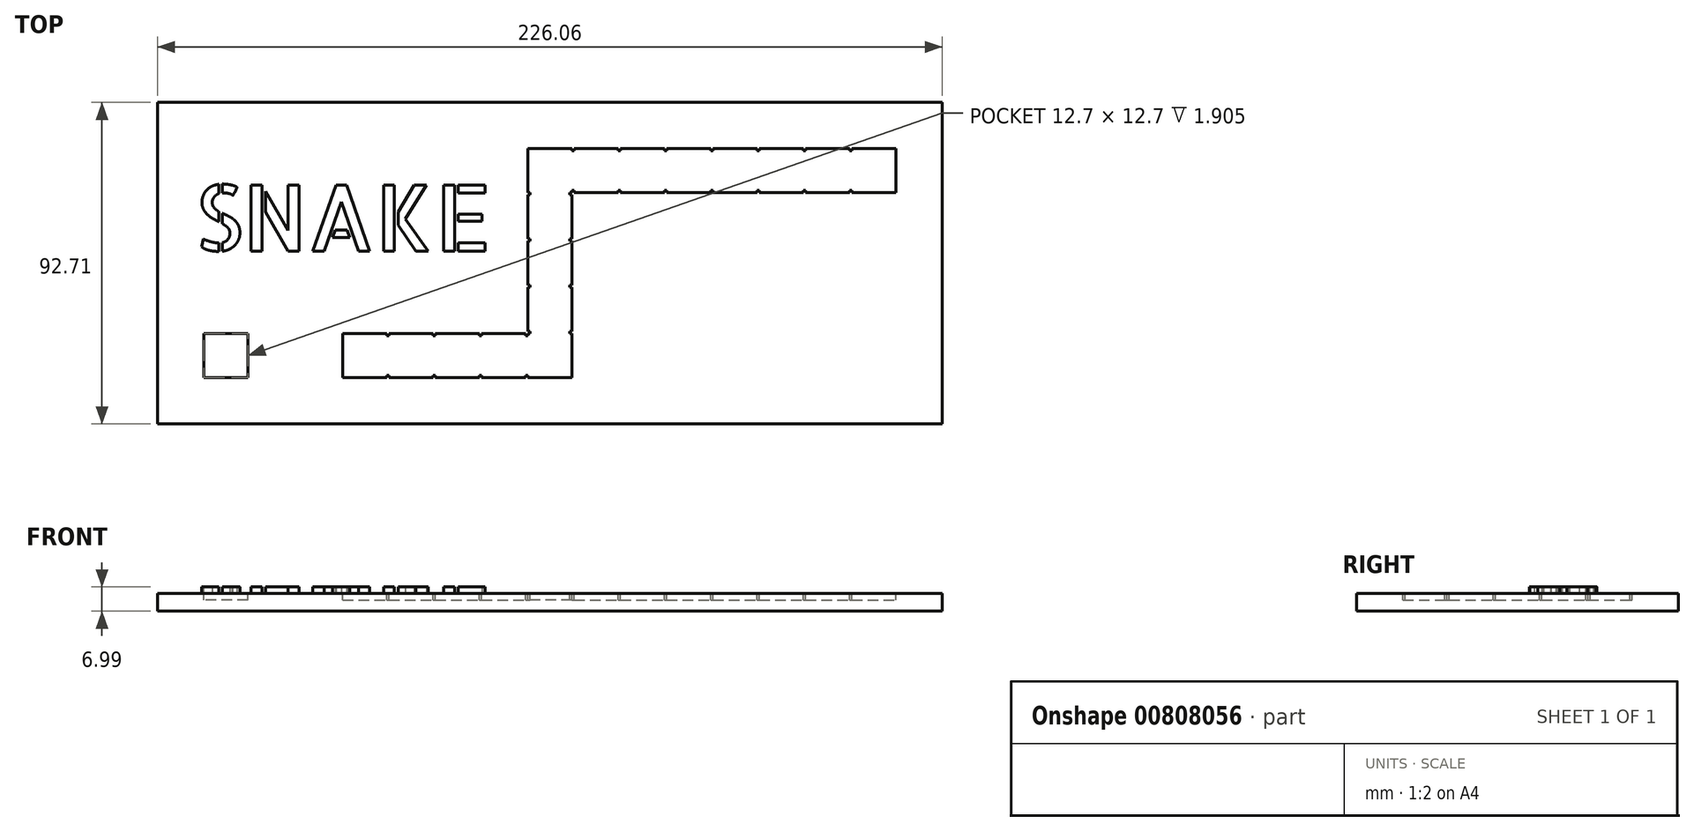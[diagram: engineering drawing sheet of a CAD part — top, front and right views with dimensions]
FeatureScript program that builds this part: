
annotation { "Feature Type Name" : "Feature", "Feature Type Description" : "" }
export const myFeature = defineFeature(function(context is Context, id is Id, definition is map)
    precondition{}
    {
        {
            var Q0;
            Q0=qCreatedBy(makeId("Top.planeOp"),FACE);
            var sketch = newSketch(context, id + "F0", { "sketchPlane" : qUnion([Q0])});
            skLineSegment(sketch, "E0.bottom", {"start": v(-132.08, 0) * mm, "end": v(-106.68, 0) * mm});
            skLineSegment(sketch, "E0.top", {"start": v(-132.08, 25.4) * mm, "end": v(-106.68, 25.4) * mm});
            skLineSegment(sketch, "E0.left", {"start": v(-132.08, 0) * mm, "end": v(-132.08, 25.4) * mm});
            skLineSegment(sketch, "E0.right", {"start": v(-106.68, 0) * mm, "end": v(-106.68, 25.4) * mm});
            skLineSegment(sketch, "E1.bottom", {"start": v(-106.68, 24.13) * mm, "end": v(-105.41, 24.13) * mm});
            skLineSegment(sketch, "E1.top", {"start": v(-106.68, 1.27) * mm, "end": v(-105.41, 1.27) * mm});
            skLineSegment(sketch, "E1.left", {"start": v(-106.68, 24.13) * mm, "end": v(-106.68, 1.27) * mm});
            skLineSegment(sketch, "E1.right", {"start": v(-105.41, 24.13) * mm, "end": v(-105.41, 1.27) * mm});
            skLineSegment(sketch, "E2", {"start": v(-106.68, 25.4) * mm, "end": v(-106.68, 24.13) * mm});
            skLineSegment(sketch, "E3", {"start": v(-106.68, 0) * mm, "end": v(-106.68, 1.27) * mm});
            skLineSegment(sketch, "E4.bottom", {"start": v(-105.41, 0) * mm, "end": v(-80.01, 0) * mm});
            skLineSegment(sketch, "E4.top", {"start": v(-105.41, 25.4) * mm, "end": v(-80.01, 25.4) * mm});
            skLineSegment(sketch, "E4.left", {"start": v(-105.41, 0) * mm, "end": v(-105.41, 25.4) * mm});
            skLineSegment(sketch, "E4.right", {"start": v(-80.01, 0) * mm, "end": v(-80.01, 25.4) * mm});
            skLineSegment(sketch, "E5.bottom", {"start": v(-80.01, 24.13) * mm, "end": v(-78.74, 24.13) * mm});
            skLineSegment(sketch, "E5.top", {"start": v(-80.01, 1.27) * mm, "end": v(-78.74, 1.27) * mm});
            skLineSegment(sketch, "E5.left", {"start": v(-80.01, 24.13) * mm, "end": v(-80.01, 1.27) * mm});
            skLineSegment(sketch, "E5.right", {"start": v(-78.74, 24.13) * mm, "end": v(-78.74, 1.27) * mm});
            skLineSegment(sketch, "E6", {"start": v(-80.01, 25.4) * mm, "end": v(-80.01, 24.13) * mm});
            skLineSegment(sketch, "E7", {"start": v(-80.01, 0) * mm, "end": v(-80.01, 1.27) * mm});
            skLineSegment(sketch, "E8.bottom", {"start": v(-78.74, 0) * mm, "end": v(-53.34, 0) * mm});
            skLineSegment(sketch, "E8.top", {"start": v(-78.74, 25.4) * mm, "end": v(-53.34, 25.4) * mm});
            skLineSegment(sketch, "E8.left", {"start": v(-78.74, 0) * mm, "end": v(-78.74, 25.4) * mm});
            skLineSegment(sketch, "E8.right", {"start": v(-53.34, 0) * mm, "end": v(-53.34, 25.4) * mm});
            skLineSegment(sketch, "E9.bottom", {"start": v(-53.34, 24.13) * mm, "end": v(-52.07, 24.13) * mm});
            skLineSegment(sketch, "E9.top", {"start": v(-53.34, 1.27) * mm, "end": v(-52.07, 1.27) * mm});
            skLineSegment(sketch, "E9.left", {"start": v(-53.34, 24.13) * mm, "end": v(-53.34, 1.27) * mm});
            skLineSegment(sketch, "E9.right", {"start": v(-52.07, 24.13) * mm, "end": v(-52.07, 1.27) * mm});
            skLineSegment(sketch, "E10", {"start": v(-53.34, 25.4) * mm, "end": v(-53.34, 24.13) * mm});
            skLineSegment(sketch, "E11", {"start": v(-53.34, 0) * mm, "end": v(-53.34, 1.27) * mm});
            skLineSegment(sketch, "E12.bottom", {"start": v(-52.07, 0) * mm, "end": v(-26.67, 0) * mm});
            skLineSegment(sketch, "E12.top", {"start": v(-52.07, 25.4) * mm, "end": v(-26.67, 25.4) * mm});
            skLineSegment(sketch, "E12.left", {"start": v(-52.07, 0) * mm, "end": v(-52.07, 25.4) * mm});
            skLineSegment(sketch, "E12.right", {"start": v(-26.67, 0) * mm, "end": v(-26.67, 25.4) * mm});
            skLineSegment(sketch, "E13.bottom", {"start": v(-26.67, 24.13) * mm, "end": v(-25.4, 24.13) * mm});
            skLineSegment(sketch, "E13.top", {"start": v(-26.67, 1.27) * mm, "end": v(-25.4, 1.27) * mm});
            skLineSegment(sketch, "E13.left", {"start": v(-26.67, 24.13) * mm, "end": v(-26.67, 1.27) * mm});
            skLineSegment(sketch, "E13.right", {"start": v(-25.4, 24.13) * mm, "end": v(-25.4, 1.27) * mm});
            skLineSegment(sketch, "E14", {"start": v(-26.67, 25.4) * mm, "end": v(-26.67, 24.13) * mm});
            skLineSegment(sketch, "E15", {"start": v(-26.67, 0) * mm, "end": v(-26.67, 1.27) * mm});
            skLineSegment(sketch, "E16.bottom", {"start": v(0, 0) * mm, "end": v(0, 25.4) * mm});
            skLineSegment(sketch, "E16.top", {"start": v(-25.4, 0) * mm, "end": v(-25.4, 25.4) * mm});
            skLineSegment(sketch, "E16.left", {"start": v(0, 0) * mm, "end": v(-25.4, 0) * mm});
            skLineSegment(sketch, "E16.right", {"start": v(0, 25.4) * mm, "end": v(-25.4, 25.4) * mm});
            skLineSegment(sketch, "E17.bottom", {"start": v(-24.13, 25.4) * mm, "end": v(-24.13, 26.67) * mm});
            skLineSegment(sketch, "E17.top", {"start": v(-1.27, 25.4) * mm, "end": v(-1.27, 26.67) * mm});
            skLineSegment(sketch, "E17.left", {"start": v(-24.13, 25.4) * mm, "end": v(-1.27, 25.4) * mm});
            skLineSegment(sketch, "E17.right", {"start": v(-24.13, 26.67) * mm, "end": v(-1.27, 26.67) * mm});
            skLineSegment(sketch, "E18", {"start": v(-25.4, 25.4) * mm, "end": v(-24.13, 25.4) * mm});
            skLineSegment(sketch, "E19", {"start": v(0, 25.4) * mm, "end": v(-1.27, 25.4) * mm});
            skLineSegment(sketch, "E20.bottom", {"start": v(0, 26.67) * mm, "end": v(0, 52.07) * mm});
            skLineSegment(sketch, "E20.top", {"start": v(-25.4, 26.67) * mm, "end": v(-25.4, 52.07) * mm});
            skLineSegment(sketch, "E20.left", {"start": v(0, 26.67) * mm, "end": v(-25.4, 26.67) * mm});
            skLineSegment(sketch, "E20.right", {"start": v(0, 52.07) * mm, "end": v(-25.4, 52.07) * mm});
            skLineSegment(sketch, "E21.bottom", {"start": v(-24.13, 52.07) * mm, "end": v(-24.13, 53.34) * mm});
            skLineSegment(sketch, "E21.top", {"start": v(-1.27, 52.07) * mm, "end": v(-1.27, 53.34) * mm});
            skLineSegment(sketch, "E21.left", {"start": v(-24.13, 52.07) * mm, "end": v(-1.27, 52.07) * mm});
            skLineSegment(sketch, "E21.right", {"start": v(-24.13, 53.34) * mm, "end": v(-1.27, 53.34) * mm});
            skLineSegment(sketch, "E22", {"start": v(-25.4, 52.07) * mm, "end": v(-24.13, 52.07) * mm});
            skLineSegment(sketch, "E23", {"start": v(0, 52.07) * mm, "end": v(-1.27, 52.07) * mm});
            skLineSegment(sketch, "E24.bottom", {"start": v(0, 53.34) * mm, "end": v(0, 78.74) * mm});
            skLineSegment(sketch, "E24.top", {"start": v(-25.4, 53.34) * mm, "end": v(-25.4, 78.74) * mm});
            skLineSegment(sketch, "E24.left", {"start": v(0, 53.34) * mm, "end": v(-25.4, 53.34) * mm});
            skLineSegment(sketch, "E24.right", {"start": v(0, 78.74) * mm, "end": v(-25.4, 78.74) * mm});
            skLineSegment(sketch, "E25.bottom", {"start": v(-24.13, 78.74) * mm, "end": v(-24.13, 80) * mm});
            skLineSegment(sketch, "E25.top", {"start": v(-1.27, 78.74) * mm, "end": v(-1.27, 80) * mm});
            skLineSegment(sketch, "E25.left", {"start": v(-24.13, 78.74) * mm, "end": v(-1.27, 78.74) * mm});
            skLineSegment(sketch, "E25.right", {"start": v(-24.13, 80) * mm, "end": v(-1.27, 80) * mm});
            skLineSegment(sketch, "E26", {"start": v(-25.4, 78.74) * mm, "end": v(-24.13, 78.74) * mm});
            skLineSegment(sketch, "E27", {"start": v(0, 78.74) * mm, "end": v(-1.27, 78.74) * mm});
            skLineSegment(sketch, "E28.bottom", {"start": v(0, 80) * mm, "end": v(0, 105.4) * mm});
            skLineSegment(sketch, "E28.top", {"start": v(-25.4, 80) * mm, "end": v(-25.4, 105.4) * mm});
            skLineSegment(sketch, "E28.left", {"start": v(0, 80) * mm, "end": v(-25.4, 80) * mm});
            skLineSegment(sketch, "E28.right", {"start": v(0, 105.4) * mm, "end": v(-25.4, 105.4) * mm});
            skLineSegment(sketch, "E29.bottom", {"start": v(-24.13, 105.4) * mm, "end": v(-24.13, 106.68) * mm});
            skLineSegment(sketch, "E29.top", {"start": v(-1.27, 105.4) * mm, "end": v(-1.27, 106.68) * mm});
            skLineSegment(sketch, "E29.left", {"start": v(-24.13, 105.4) * mm, "end": v(-1.27, 105.4) * mm});
            skLineSegment(sketch, "E29.right", {"start": v(-24.13, 106.68) * mm, "end": v(-1.27, 106.68) * mm});
            skLineSegment(sketch, "E30", {"start": v(-25.4, 105.4) * mm, "end": v(-24.13, 105.4) * mm});
            skLineSegment(sketch, "E31", {"start": v(0, 105.4) * mm, "end": v(-1.27, 105.4) * mm});
            skLineSegment(sketch, "E32", {"start": v(-25.4, 1.27) * mm, "end": v(-25.4, 12.7) * mm});
            skLineSegment(sketch, "E33", {"start": v(-25.4, 12.7) * mm, "end": v(-26.67, 12.7) * mm});
            skLineSegment(sketch, "E34.bottom", {"start": v(-25.4, 106.68) * mm, "end": v(0, 106.68) * mm});
            skLineSegment(sketch, "E34.top", {"start": v(-25.4, 132.08) * mm, "end": v(0, 132.08) * mm});
            skLineSegment(sketch, "E34.left", {"start": v(-25.4, 106.68) * mm, "end": v(-25.4, 132.08) * mm});
            skLineSegment(sketch, "E34.right", {"start": v(0, 106.68) * mm, "end": v(0, 132.08) * mm});
            skLineSegment(sketch, "E35.bottom", {"start": v(0, 130.8) * mm, "end": v(1.27, 130.8) * mm});
            skLineSegment(sketch, "E35.top", {"start": v(0, 107.95) * mm, "end": v(1.27, 107.95) * mm});
            skLineSegment(sketch, "E35.left", {"start": v(0, 130.8) * mm, "end": v(0, 107.95) * mm});
            skLineSegment(sketch, "E35.right", {"start": v(1.27, 130.8) * mm, "end": v(1.27, 107.95) * mm});
            skLineSegment(sketch, "E36", {"start": v(0, 132.08) * mm, "end": v(0, 130.8) * mm});
            skLineSegment(sketch, "E37", {"start": v(0, 106.68) * mm, "end": v(0, 107.95) * mm});
            skLineSegment(sketch, "E38.bottom", {"start": v(1.27, 106.68) * mm, "end": v(26.67, 106.68) * mm});
            skLineSegment(sketch, "E38.top", {"start": v(1.27, 132.08) * mm, "end": v(26.67, 132.08) * mm});
            skLineSegment(sketch, "E38.left", {"start": v(1.27, 106.68) * mm, "end": v(1.27, 132.08) * mm});
            skLineSegment(sketch, "E38.right", {"start": v(26.67, 106.68) * mm, "end": v(26.67, 132.08) * mm});
            skLineSegment(sketch, "E39.bottom", {"start": v(26.67, 130.8) * mm, "end": v(27.94, 130.8) * mm});
            skLineSegment(sketch, "E39.top", {"start": v(26.67, 107.95) * mm, "end": v(27.94, 107.95) * mm});
            skLineSegment(sketch, "E39.left", {"start": v(26.67, 130.8) * mm, "end": v(26.67, 107.95) * mm});
            skLineSegment(sketch, "E39.right", {"start": v(27.94, 130.8) * mm, "end": v(27.94, 107.95) * mm});
            skLineSegment(sketch, "E40", {"start": v(26.67, 132.08) * mm, "end": v(26.67, 130.8) * mm});
            skLineSegment(sketch, "E41", {"start": v(26.67, 106.68) * mm, "end": v(26.67, 107.95) * mm});
            skLineSegment(sketch, "E42.bottom", {"start": v(27.94, 106.68) * mm, "end": v(53.34, 106.68) * mm});
            skLineSegment(sketch, "E42.top", {"start": v(27.94, 132.08) * mm, "end": v(53.34, 132.08) * mm});
            skLineSegment(sketch, "E42.left", {"start": v(27.94, 106.68) * mm, "end": v(27.94, 132.08) * mm});
            skLineSegment(sketch, "E42.right", {"start": v(53.34, 106.68) * mm, "end": v(53.34, 132.08) * mm});
            skLineSegment(sketch, "E43.bottom", {"start": v(53.34, 130.8) * mm, "end": v(54.6, 130.8) * mm});
            skLineSegment(sketch, "E43.top", {"start": v(53.34, 107.95) * mm, "end": v(54.6, 107.95) * mm});
            skLineSegment(sketch, "E43.left", {"start": v(53.34, 130.8) * mm, "end": v(53.34, 107.95) * mm});
            skLineSegment(sketch, "E43.right", {"start": v(54.6, 130.8) * mm, "end": v(54.6, 107.95) * mm});
            skLineSegment(sketch, "E44", {"start": v(53.34, 132.08) * mm, "end": v(53.34, 130.8) * mm});
            skLineSegment(sketch, "E45", {"start": v(53.34, 106.68) * mm, "end": v(53.34, 107.95) * mm});
            skLineSegment(sketch, "E46.bottom", {"start": v(54.6, 106.68) * mm, "end": v(80, 106.68) * mm});
            skLineSegment(sketch, "E46.top", {"start": v(54.6, 132.08) * mm, "end": v(80, 132.08) * mm});
            skLineSegment(sketch, "E46.left", {"start": v(54.6, 106.68) * mm, "end": v(54.6, 132.08) * mm});
            skLineSegment(sketch, "E46.right", {"start": v(80, 106.68) * mm, "end": v(80, 132.08) * mm});
            skLineSegment(sketch, "E47.bottom", {"start": v(80, 130.8) * mm, "end": v(81.28, 130.8) * mm});
            skLineSegment(sketch, "E47.top", {"start": v(80, 107.95) * mm, "end": v(81.28, 107.95) * mm});
            skLineSegment(sketch, "E47.left", {"start": v(80, 130.8) * mm, "end": v(80, 107.95) * mm});
            skLineSegment(sketch, "E47.right", {"start": v(81.28, 130.8) * mm, "end": v(81.28, 107.95) * mm});
            skLineSegment(sketch, "E48", {"start": v(80, 132.08) * mm, "end": v(80, 130.8) * mm});
            skLineSegment(sketch, "E49", {"start": v(80, 106.68) * mm, "end": v(80, 107.95) * mm});
            skLineSegment(sketch, "E50.bottom", {"start": v(81.28, 106.68) * mm, "end": v(106.68, 106.68) * mm});
            skLineSegment(sketch, "E50.top", {"start": v(81.28, 132.08) * mm, "end": v(106.68, 132.08) * mm});
            skLineSegment(sketch, "E50.left", {"start": v(81.28, 106.68) * mm, "end": v(81.28, 132.08) * mm});
            skLineSegment(sketch, "E50.right", {"start": v(106.68, 106.68) * mm, "end": v(106.68, 132.08) * mm});
            skLineSegment(sketch, "E51.bottom", {"start": v(106.68, 130.8) * mm, "end": v(107.95, 130.8) * mm});
            skLineSegment(sketch, "E51.top", {"start": v(106.68, 107.95) * mm, "end": v(107.95, 107.95) * mm});
            skLineSegment(sketch, "E51.left", {"start": v(106.68, 130.8) * mm, "end": v(106.68, 107.95) * mm});
            skLineSegment(sketch, "E51.right", {"start": v(107.95, 130.8) * mm, "end": v(107.95, 107.95) * mm});
            skLineSegment(sketch, "E52", {"start": v(106.68, 132.08) * mm, "end": v(106.68, 130.8) * mm});
            skLineSegment(sketch, "E53", {"start": v(106.68, 106.68) * mm, "end": v(106.68, 107.95) * mm});
            skLineSegment(sketch, "E54.bottom", {"start": v(107.95, 106.68) * mm, "end": v(133.35, 106.68) * mm});
            skLineSegment(sketch, "E54.top", {"start": v(107.95, 132.08) * mm, "end": v(133.35, 132.08) * mm});
            skLineSegment(sketch, "E54.left", {"start": v(107.95, 106.68) * mm, "end": v(107.95, 132.08) * mm});
            skLineSegment(sketch, "E54.right", {"start": v(133.35, 106.68) * mm, "end": v(133.35, 132.08) * mm});
            skLineSegment(sketch, "E55.bottom", {"start": v(133.35, 130.8) * mm, "end": v(134.62, 130.8) * mm});
            skLineSegment(sketch, "E55.top", {"start": v(133.35, 107.95) * mm, "end": v(134.62, 107.95) * mm});
            skLineSegment(sketch, "E55.left", {"start": v(133.35, 130.8) * mm, "end": v(133.35, 107.95) * mm});
            skLineSegment(sketch, "E55.right", {"start": v(134.62, 130.8) * mm, "end": v(134.62, 107.95) * mm});
            skLineSegment(sketch, "E56", {"start": v(133.35, 132.08) * mm, "end": v(133.35, 130.8) * mm});
            skLineSegment(sketch, "E57", {"start": v(133.35, 106.68) * mm, "end": v(133.35, 107.95) * mm});
            skLineSegment(sketch, "E58.bottom", {"start": v(134.62, 106.68) * mm, "end": v(160.02, 106.68) * mm});
            skLineSegment(sketch, "E58.top", {"start": v(134.62, 132.08) * mm, "end": v(160.02, 132.08) * mm});
            skLineSegment(sketch, "E58.left", {"start": v(134.62, 106.68) * mm, "end": v(134.62, 132.08) * mm});
            skLineSegment(sketch, "E58.right", {"start": v(160.02, 106.68) * mm, "end": v(160.02, 132.08) * mm});
            skLineSegment(sketch, "E59.bottom", {"start": v(160.02, 130.8) * mm, "end": v(161.29, 130.8) * mm});
            skLineSegment(sketch, "E59.top", {"start": v(160.02, 107.95) * mm, "end": v(161.29, 107.95) * mm});
            skLineSegment(sketch, "E59.left", {"start": v(160.02, 130.8) * mm, "end": v(160.02, 107.95) * mm});
            skLineSegment(sketch, "E59.right", {"start": v(161.29, 130.8) * mm, "end": v(161.29, 107.95) * mm});
            skLineSegment(sketch, "E60", {"start": v(160.02, 132.08) * mm, "end": v(160.02, 130.8) * mm});
            skLineSegment(sketch, "E61", {"start": v(160.02, 106.68) * mm, "end": v(160.02, 107.95) * mm});
            skLineSegment(sketch, "E62.bottom", {"start": v(161.29, 106.68) * mm, "end": v(186.69, 106.68) * mm});
            skLineSegment(sketch, "E62.top", {"start": v(161.29, 132.08) * mm, "end": v(186.7, 132.08) * mm});
            skLineSegment(sketch, "E62.left", {"start": v(161.29, 106.68) * mm, "end": v(161.29, 132.08) * mm});
            skLineSegment(sketch, "E62.right", {"start": v(186.7, 106.68) * mm, "end": v(186.7, 132.08) * mm});
            skLineSegment(sketch, "E63.left", {"start": v(186.7, 130.8) * mm, "end": v(186.7, 42.8) * mm});
            skLineSegment(sketch, "E64", {"start": v(186.7, 132.08) * mm, "end": v(186.7, 130.8) * mm});
            skLineSegment(sketch, "E65", {"start": v(186.7, 42.8) * mm, "end": v(186.7, 106.68) * mm});
            skLineSegment(sketch, "E66.bottom", {"start": v(213.36, -26.67) * mm, "end": v(-238.76, -26.67) * mm});
            skLineSegment(sketch, "E66.top", {"start": v(213.36, 158.75) * mm, "end": v(-238.76, 158.75) * mm});
            skLineSegment(sketch, "E66.left", {"start": v(213.36, -26.67) * mm, "end": v(213.36, 158.75) * mm});
            skLineSegment(sketch, "E66.right", {"start": v(-238.76, -26.67) * mm, "end": v(-238.76, 158.75) * mm});
            skLineSegment(sketch, "E67.bottom", {"start": v(-186.7, 25.4) * mm, "end": v(-212.1, 25.4) * mm});
            skLineSegment(sketch, "E67.top", {"start": v(-186.7, 0) * mm, "end": v(-212.1, 0) * mm});
            skLineSegment(sketch, "E67.left", {"start": v(-186.7, 25.4) * mm, "end": v(-186.7, 0) * mm});
            skLineSegment(sketch, "E67.right", {"start": v(-212.1, 25.4) * mm, "end": v(-212.1, 0) * mm});
            skText(sketch, "E68", { "text": "SNAKE", "fontName": "AllertaStencil-Regular.ttf"});
            skLineSegment(sketch, "E69", {"start": v(-217.6, 73.02) * mm, "end": v(-238.76, 73.02) * mm});
            skLineSegment(sketch, "E70", {"start": v(-46.57, 111.12) * mm, "end": v(-25.4, 111.12) * mm});
            skLineSegment(sketch, "E71", {"start": v(-132.08, 111.12) * mm, "end": v(-132.08, 158.75) * mm});
            skLineSegment(sketch, "E72", {"start": v(-132.08, 25.4) * mm, "end": v(-132.08, 73.02) * mm});
            const initialGuessF0  = {"E68": [-0.2176, 0.07302, 1, 0, 0.0381]};
            skSetInitialGuess(sketch, initialGuessF0);
            skSolve(sketch);
        }
        {
            var Q0;
            {var subQ3=sQuery(id+"F0.wireOp",EDGE,"E28.bottom");Q0=makeQuery(id+"F0.imprint","IMPRINT",FACE,{"disambiguationData":[TD([[makeQuery(id+"F0.imprint","IMPRINT",EDGE,{"derivedFrom":subQ3}),1.0]])]});}
            var Q1;
            Q1=makeQuery(id+"F0.imprint","IMPRINT",FACE,{"disambiguationData":[TD([[makeQuery(id+"F0.imprint","IMPRINT",EDGE,{"derivedFrom":sQuery(id+"F0.wireOp",EDGE,"E68.sketch_text.stroke-72")}),-1.0]])]});
            var Q2;
            Q2=makeQuery(id+"F0.imprint","IMPRINT",FACE,{"disambiguationData":[TD([[makeQuery(id+"F0.imprint","IMPRINT",EDGE,{"derivedFrom":sQuery(id+"F0.wireOp",EDGE,"E68.sketch_text.stroke-76")}),-1.0]])]});
            var Q3;
            {var subQ3=sQuery(id+"F0.wireOp",EDGE,"E24.bottom");Q3=makeQuery(id+"F0.imprint","IMPRINT",FACE,{"disambiguationData":[TD([[makeQuery(id+"F0.imprint","IMPRINT",EDGE,{"derivedFrom":subQ3}),1.0]])]});}
            var Q4;
            {var subQ3=sQuery(id+"F0.wireOp",EDGE,"E58.bottom");Q4=makeQuery(id+"F0.imprint","IMPRINT",FACE,{"disambiguationData":[TD([[makeQuery(id+"F0.imprint","IMPRINT",EDGE,{"derivedFrom":subQ3}),1.0]])]});}
            var Q5;
            {var subQ3=sQuery(id+"F0.wireOp",EDGE,"E62.bottom");Q5=makeQuery(id+"F0.imprint","IMPRINT",FACE,{"disambiguationData":[TD([[makeQuery(id+"F0.imprint","IMPRINT",EDGE,{"derivedFrom":subQ3}),1.0]])]});}
            var Q6;
            {var subQ3=sQuery(id+"F0.wireOp",EDGE,"E38.bottom");Q6=makeQuery(id+"F0.imprint","IMPRINT",FACE,{"disambiguationData":[TD([[makeQuery(id+"F0.imprint","IMPRINT",EDGE,{"derivedFrom":subQ3}),1.0]])]});}
            var Q7;
            Q7=makeQuery(id+"F0.imprint","IMPRINT",FACE,{"disambiguationData":[TD([[makeQuery(id+"F0.imprint","IMPRINT",EDGE,{"derivedFrom":sQuery(id+"F0.wireOp",EDGE,"E0.bottom")}),-1.0]])]});
            var Q8;
            {var subQ0=sQuery(id+"F0.wireOp",EDGE,"E34.top");Q8=makeQuery(id+"F0.imprint","IMPRINT",FACE,{"disambiguationData":[TD([[makeQuery(id+"F0.imprint","IMPRINT",EDGE,{"derivedFrom":subQ0}),-1.0]])]});}
            var Q9;
            {var subQ3=sQuery(id+"F0.wireOp",EDGE,"E42.bottom");Q9=makeQuery(id+"F0.imprint","IMPRINT",FACE,{"disambiguationData":[TD([[makeQuery(id+"F0.imprint","IMPRINT",EDGE,{"derivedFrom":subQ3}),1.0]])]});}
            var Q10;
            Q10=makeQuery(id+"F0.imprint","IMPRINT",FACE,{"disambiguationData":[TD([[makeQuery(id+"F0.imprint","IMPRINT",EDGE,{"derivedFrom":sQuery(id+"F0.wireOp",EDGE,"E68.sketch_text.stroke-83")}),-1.0]])]});
            var Q11;
            {var subQ3=sQuery(id+"F0.wireOp",EDGE,"E4.bottom");Q11=makeQuery(id+"F0.imprint","IMPRINT",FACE,{"disambiguationData":[TD([[makeQuery(id+"F0.imprint","IMPRINT",EDGE,{"derivedFrom":subQ3}),1.0]])]});}
            var Q12;
            {var subQ3=sQuery(id+"F0.wireOp",EDGE,"E46.bottom");Q12=makeQuery(id+"F0.imprint","IMPRINT",FACE,{"disambiguationData":[TD([[makeQuery(id+"F0.imprint","IMPRINT",EDGE,{"derivedFrom":subQ3}),1.0]])]});}
            var Q13;
            {var subQ3=sQuery(id+"F0.wireOp",EDGE,"E54.bottom");Q13=makeQuery(id+"F0.imprint","IMPRINT",FACE,{"disambiguationData":[TD([[makeQuery(id+"F0.imprint","IMPRINT",EDGE,{"derivedFrom":subQ3}),1.0]])]});}
            var Q14;
            {var subQ3=sQuery(id+"F0.wireOp",EDGE,"E8.bottom");Q14=makeQuery(id+"F0.imprint","IMPRINT",FACE,{"disambiguationData":[TD([[makeQuery(id+"F0.imprint","IMPRINT",EDGE,{"derivedFrom":subQ3}),1.0]])]});}
            var Q15;
            {var subQ3=sQuery(id+"F0.wireOp",EDGE,"E20.bottom");Q15=makeQuery(id+"F0.imprint","IMPRINT",FACE,{"disambiguationData":[TD([[makeQuery(id+"F0.imprint","IMPRINT",EDGE,{"derivedFrom":subQ3}),1.0]])]});}
            var Q16;
            Q16=makeQuery(id+"F0.imprint","IMPRINT",FACE,{"disambiguationData":[TD([[makeQuery(id+"F0.imprint","IMPRINT",EDGE,{"derivedFrom":sQuery(id+"F0.wireOp",EDGE,"E0.bottom")}),1.0]])]});
            var Q17;
            Q17=makeQuery(id+"F0.imprint","IMPRINT",FACE,{"disambiguationData":[TD([[makeQuery(id+"F0.imprint","IMPRINT",EDGE,{"derivedFrom":sQuery(id+"F0.wireOp",EDGE,"E68.sketch_text.stroke-95")}),-1.0]])]});
            var Q18;
            Q18=makeQuery(id+"F0.imprint","IMPRINT",FACE,{"disambiguationData":[TD([[makeQuery(id+"F0.imprint","IMPRINT",EDGE,{"derivedFrom":sQuery(id+"F0.wireOp",EDGE,"E67.bottom")}),1.0]])]});
            var Q19;
            Q19=makeQuery(id+"F0.imprint","IMPRINT",FACE,{"disambiguationData":[TD([[makeQuery(id+"F0.imprint","IMPRINT",EDGE,{"derivedFrom":sQuery(id+"F0.wireOp",EDGE,"E68.sketch_text.stroke-50")}),-1.0]])]});
            var Q20;
            Q20=makeQuery(id+"F0.imprint","IMPRINT",FACE,{"disambiguationData":[TD([[makeQuery(id+"F0.imprint","IMPRINT",EDGE,{"derivedFrom":sQuery(id+"F0.wireOp",EDGE,"E68.sketch_text.stroke-57")}),-1.0]])]});
            var Q21;
            Q21=makeQuery(id+"F0.imprint","IMPRINT",FACE,{"disambiguationData":[TD([[makeQuery(id+"F0.imprint","IMPRINT",EDGE,{"derivedFrom":sQuery(id+"F0.wireOp",EDGE,"E68.sketch_text.stroke-61")}),-1.0]])]});
            var Q22;
            Q22=makeQuery(id+"F0.imprint","IMPRINT",FACE,{"disambiguationData":[TD([[makeQuery(id+"F0.imprint","IMPRINT",EDGE,{"derivedFrom":sQuery(id+"F0.wireOp",EDGE,"E16.bottom")}),1.0]])]});
            var Q23;
            Q23=makeQuery(id+"F0.imprint","IMPRINT",FACE,{"disambiguationData":[TD([[makeQuery(id+"F0.imprint","IMPRINT",EDGE,{"derivedFrom":sQuery(id+"F0.wireOp",EDGE,"E68.sketch_text.stroke-68")}),-1.0]])]});
            var Q24;
            Q24=makeQuery(id+"F0.imprint","IMPRINT",FACE,{"disambiguationData":[TD([[makeQuery(id+"F0.imprint","IMPRINT",EDGE,{"derivedFrom":sQuery(id+"F0.wireOp",EDGE,"E68.sketch_text.stroke-87")}),-1.0]])]});
            var Q25;
            {var subQ3=sQuery(id+"F0.wireOp",EDGE,"E50.bottom");Q25=makeQuery(id+"F0.imprint","IMPRINT",FACE,{"disambiguationData":[TD([[makeQuery(id+"F0.imprint","IMPRINT",EDGE,{"derivedFrom":subQ3}),1.0]])]});}
            var Q26;
            Q26=makeQuery(id+"F0.imprint","IMPRINT",FACE,{"disambiguationData":[TD([[makeQuery(id+"F0.imprint","IMPRINT",EDGE,{"derivedFrom":sQuery(id+"F0.wireOp",EDGE,"E68.sketch_text.stroke-91")}),-1.0]])]});
            var Q27;
            Q27=makeQuery(id+"F0.imprint","IMPRINT",FACE,{"disambiguationData":[TD([[makeQuery(id+"F0.imprint","IMPRINT",EDGE,{"derivedFrom":sQuery(id+"F0.wireOp",EDGE,"E68.sketch_text.stroke-0")}),-1.0]])]});
            var Q28;
            Q28=makeQuery(id+"F0.imprint","IMPRINT",FACE,{"disambiguationData":[TD([[makeQuery(id+"F0.imprint","IMPRINT",EDGE,{"derivedFrom":sQuery(id+"F0.wireOp",EDGE,"E68.sketch_text.stroke-11")}),-1.0]])]});
            var Q29;
            Q29=makeQuery(id+"F0.imprint","IMPRINT",FACE,{"disambiguationData":[TD([[makeQuery(id+"F0.imprint","IMPRINT",EDGE,{"derivedFrom":sQuery(id+"F0.wireOp",EDGE,"E68.sketch_text.stroke-25")}),-1.0]])]});
            var Q30;
            Q30=makeQuery(id+"F0.imprint","IMPRINT",FACE,{"disambiguationData":[TD([[makeQuery(id+"F0.imprint","IMPRINT",EDGE,{"derivedFrom":sQuery(id+"F0.wireOp",EDGE,"E68.sketch_text.stroke-37")}),-1.0]])]});
            var Q31;
            {var subQ3=sQuery(id+"F0.wireOp",EDGE,"E12.bottom");Q31=makeQuery(id+"F0.imprint","IMPRINT",FACE,{"disambiguationData":[TD([[makeQuery(id+"F0.imprint","IMPRINT",EDGE,{"derivedFrom":subQ3}),1.0]])]});}
            var Q32;
            {var subQ0=sQuery(id+"F0.wireOp",EDGE,"E35.bottom");Q32=makeQuery(id+"F0.imprint","IMPRINT",FACE,{"disambiguationData":[TD([[makeQuery(id+"F0.imprint","IMPRINT",EDGE,{"derivedFrom":subQ0}),-1.0]])]});}
            var Q33;
            {var subQ0=sQuery(id+"F0.wireOp",EDGE,"E39.bottom");Q33=makeQuery(id+"F0.imprint","IMPRINT",FACE,{"disambiguationData":[TD([[makeQuery(id+"F0.imprint","IMPRINT",EDGE,{"derivedFrom":subQ0}),-1.0]])]});}
            var Q34;
            {var subQ0=sQuery(id+"F0.wireOp",EDGE,"E59.bottom");Q34=makeQuery(id+"F0.imprint","IMPRINT",FACE,{"disambiguationData":[TD([[makeQuery(id+"F0.imprint","IMPRINT",EDGE,{"derivedFrom":subQ0}),-1.0]])]});}
            var Q35;
            {var subQ0=sQuery(id+"F0.wireOp",EDGE,"E1.bottom");Q35=makeQuery(id+"F0.imprint","IMPRINT",FACE,{"disambiguationData":[TD([[makeQuery(id+"F0.imprint","IMPRINT",EDGE,{"derivedFrom":subQ0}),-1.0]])]});}
            var Q36;
            {var subQ0=sQuery(id+"F0.wireOp",EDGE,"E43.bottom");Q36=makeQuery(id+"F0.imprint","IMPRINT",FACE,{"disambiguationData":[TD([[makeQuery(id+"F0.imprint","IMPRINT",EDGE,{"derivedFrom":subQ0}),-1.0]])]});}
            var Q37;
            {var subQ0=sQuery(id+"F0.wireOp",EDGE,"E5.bottom");Q37=makeQuery(id+"F0.imprint","IMPRINT",FACE,{"disambiguationData":[TD([[makeQuery(id+"F0.imprint","IMPRINT",EDGE,{"derivedFrom":subQ0}),-1.0]])]});}
            var Q38;
            {var subQ0=sQuery(id+"F0.wireOp",EDGE,"E47.bottom");Q38=makeQuery(id+"F0.imprint","IMPRINT",FACE,{"disambiguationData":[TD([[makeQuery(id+"F0.imprint","IMPRINT",EDGE,{"derivedFrom":subQ0}),-1.0]])]});}
            var Q39;
            {var subQ0=sQuery(id+"F0.wireOp",EDGE,"E9.bottom");Q39=makeQuery(id+"F0.imprint","IMPRINT",FACE,{"disambiguationData":[TD([[makeQuery(id+"F0.imprint","IMPRINT",EDGE,{"derivedFrom":subQ0}),-1.0]])]});}
            var Q40;
            {var subQ0=sQuery(id+"F0.wireOp",EDGE,"E55.bottom");Q40=makeQuery(id+"F0.imprint","IMPRINT",FACE,{"disambiguationData":[TD([[makeQuery(id+"F0.imprint","IMPRINT",EDGE,{"derivedFrom":subQ0}),-1.0]])]});}
            var Q41;
            {var subQ0=sQuery(id+"F0.wireOp",EDGE,"E21.bottom");Q41=makeQuery(id+"F0.imprint","IMPRINT",FACE,{"disambiguationData":[TD([[makeQuery(id+"F0.imprint","IMPRINT",EDGE,{"derivedFrom":subQ0}),-1.0]])]});}
            var Q42;
            {var subQ0=sQuery(id+"F0.wireOp",EDGE,"E51.bottom");Q42=makeQuery(id+"F0.imprint","IMPRINT",FACE,{"disambiguationData":[TD([[makeQuery(id+"F0.imprint","IMPRINT",EDGE,{"derivedFrom":subQ0}),-1.0]])]});}
            var Q43;
            {var subQ0=sQuery(id+"F0.wireOp",EDGE,"E13.bottom");Q43=makeQuery(id+"F0.imprint","IMPRINT",FACE,{"disambiguationData":[TD([[makeQuery(id+"F0.imprint","IMPRINT",EDGE,{"derivedFrom":subQ0}),-1.0]])]});}
            var Q44;
            {var subQ0=sQuery(id+"F0.wireOp",EDGE,"E13.top");Q44=makeQuery(id+"F0.imprint","IMPRINT",FACE,{"disambiguationData":[TD([[makeQuery(id+"F0.imprint","IMPRINT",EDGE,{"derivedFrom":subQ0}),1.0]])]});}
            var Q45;
            {var subQ0=sQuery(id+"F0.wireOp",EDGE,"E17.bottom");Q45=makeQuery(id+"F0.imprint","IMPRINT",FACE,{"disambiguationData":[TD([[makeQuery(id+"F0.imprint","IMPRINT",EDGE,{"derivedFrom":subQ0}),-1.0]])]});}
            var Q46;
            {var subQ0=sQuery(id+"F0.wireOp",EDGE,"E25.bottom");Q46=makeQuery(id+"F0.imprint","IMPRINT",FACE,{"disambiguationData":[TD([[makeQuery(id+"F0.imprint","IMPRINT",EDGE,{"derivedFrom":subQ0}),-1.0]])]});}
            var Q47;
            {var subQ0=sQuery(id+"F0.wireOp",EDGE,"E29.bottom");Q47=makeQuery(id+"F0.imprint","IMPRINT",FACE,{"disambiguationData":[TD([[makeQuery(id+"F0.imprint","IMPRINT",EDGE,{"derivedFrom":subQ0}),-1.0]])]});}
            extrude(context, id + "F1", {"entities" : qUnion([Q0, Q1, Q2, Q3, Q4, Q5, Q6, Q7, Q8, Q9, Q10, Q11, Q12, Q13, Q14, Q15, Q16, Q17, Q18, Q19, Q20, Q21, Q22, Q23, Q24, Q25, Q26, Q27, Q28, Q29, Q30, Q31, Q32, Q33, Q34, Q35, Q36, Q37, Q38, Q39, Q40, Q41, Q42, Q43, Q44, Q45, Q46, Q47]), "oppositeDirection" : true, "depth" : 10.16 * mm, "offsetDistance" : 25.4 * mm});
        }
        {
            var Q0;
            {var subQ3=sQuery(id+"F0.wireOp",EDGE,"E28.bottom");Q0=makeQuery(id+"F0.imprint","IMPRINT",FACE,{"disambiguationData":[TD([[makeQuery(id+"F0.imprint","IMPRINT",EDGE,{"derivedFrom":subQ3}),1.0]])]});}
            var Q1;
            Q1=makeQuery(id+"F0.imprint","IMPRINT",FACE,{"disambiguationData":[TD([[makeQuery(id+"F0.imprint","IMPRINT",EDGE,{"derivedFrom":sQuery(id+"F0.wireOp",EDGE,"E16.bottom")}),1.0]])]});
            var Q2;
            Q2=makeQuery(id+"F0.imprint","IMPRINT",FACE,{"disambiguationData":[TD([[makeQuery(id+"F0.imprint","IMPRINT",EDGE,{"derivedFrom":sQuery(id+"F0.wireOp",EDGE,"E68.sketch_text.stroke-72")}),-1.0]])]});
            var Q3;
            Q3=makeQuery(id+"F0.imprint","IMPRINT",FACE,{"disambiguationData":[TD([[makeQuery(id+"F0.imprint","IMPRINT",EDGE,{"derivedFrom":sQuery(id+"F0.wireOp",EDGE,"E68.sketch_text.stroke-76")}),-1.0]])]});
            var Q4;
            {var subQ3=sQuery(id+"F0.wireOp",EDGE,"E24.bottom");Q4=makeQuery(id+"F0.imprint","IMPRINT",FACE,{"disambiguationData":[TD([[makeQuery(id+"F0.imprint","IMPRINT",EDGE,{"derivedFrom":subQ3}),1.0]])]});}
            var Q5;
            {var subQ3=sQuery(id+"F0.wireOp",EDGE,"E58.bottom");Q5=makeQuery(id+"F0.imprint","IMPRINT",FACE,{"disambiguationData":[TD([[makeQuery(id+"F0.imprint","IMPRINT",EDGE,{"derivedFrom":subQ3}),1.0]])]});}
            var Q6;
            {var subQ3=sQuery(id+"F0.wireOp",EDGE,"E62.bottom");Q6=makeQuery(id+"F0.imprint","IMPRINT",FACE,{"disambiguationData":[TD([[makeQuery(id+"F0.imprint","IMPRINT",EDGE,{"derivedFrom":subQ3}),1.0]])]});}
            var Q7;
            {var subQ3=sQuery(id+"F0.wireOp",EDGE,"E38.bottom");Q7=makeQuery(id+"F0.imprint","IMPRINT",FACE,{"disambiguationData":[TD([[makeQuery(id+"F0.imprint","IMPRINT",EDGE,{"derivedFrom":subQ3}),1.0]])]});}
            var Q8;
            Q8=makeQuery(id+"F0.imprint","IMPRINT",FACE,{"disambiguationData":[TD([[makeQuery(id+"F0.imprint","IMPRINT",EDGE,{"derivedFrom":sQuery(id+"F0.wireOp",EDGE,"E68.sketch_text.stroke-68")}),-1.0]])]});
            var Q9;
            {var subQ0=sQuery(id+"F0.wireOp",EDGE,"E34.top");Q9=makeQuery(id+"F0.imprint","IMPRINT",FACE,{"disambiguationData":[TD([[makeQuery(id+"F0.imprint","IMPRINT",EDGE,{"derivedFrom":subQ0}),-1.0]])]});}
            var Q10;
            {var subQ3=sQuery(id+"F0.wireOp",EDGE,"E42.bottom");Q10=makeQuery(id+"F0.imprint","IMPRINT",FACE,{"disambiguationData":[TD([[makeQuery(id+"F0.imprint","IMPRINT",EDGE,{"derivedFrom":subQ3}),1.0]])]});}
            var Q11;
            Q11=makeQuery(id+"F0.imprint","IMPRINT",FACE,{"disambiguationData":[TD([[makeQuery(id+"F0.imprint","IMPRINT",EDGE,{"derivedFrom":sQuery(id+"F0.wireOp",EDGE,"E68.sketch_text.stroke-83")}),-1.0]])]});
            var Q12;
            {var subQ3=sQuery(id+"F0.wireOp",EDGE,"E4.bottom");Q12=makeQuery(id+"F0.imprint","IMPRINT",FACE,{"disambiguationData":[TD([[makeQuery(id+"F0.imprint","IMPRINT",EDGE,{"derivedFrom":subQ3}),1.0]])]});}
            var Q13;
            Q13=makeQuery(id+"F0.imprint","IMPRINT",FACE,{"disambiguationData":[TD([[makeQuery(id+"F0.imprint","IMPRINT",EDGE,{"derivedFrom":sQuery(id+"F0.wireOp",EDGE,"E68.sketch_text.stroke-87")}),-1.0]])]});
            var Q14;
            {var subQ3=sQuery(id+"F0.wireOp",EDGE,"E46.bottom");Q14=makeQuery(id+"F0.imprint","IMPRINT",FACE,{"disambiguationData":[TD([[makeQuery(id+"F0.imprint","IMPRINT",EDGE,{"derivedFrom":subQ3}),1.0]])]});}
            var Q15;
            {var subQ3=sQuery(id+"F0.wireOp",EDGE,"E54.bottom");Q15=makeQuery(id+"F0.imprint","IMPRINT",FACE,{"disambiguationData":[TD([[makeQuery(id+"F0.imprint","IMPRINT",EDGE,{"derivedFrom":subQ3}),1.0]])]});}
            var Q16;
            {var subQ3=sQuery(id+"F0.wireOp",EDGE,"E8.bottom");Q16=makeQuery(id+"F0.imprint","IMPRINT",FACE,{"disambiguationData":[TD([[makeQuery(id+"F0.imprint","IMPRINT",EDGE,{"derivedFrom":subQ3}),1.0]])]});}
            var Q17;
            {var subQ3=sQuery(id+"F0.wireOp",EDGE,"E20.bottom");Q17=makeQuery(id+"F0.imprint","IMPRINT",FACE,{"disambiguationData":[TD([[makeQuery(id+"F0.imprint","IMPRINT",EDGE,{"derivedFrom":subQ3}),1.0]])]});}
            var Q18;
            {var subQ3=sQuery(id+"F0.wireOp",EDGE,"E50.bottom");Q18=makeQuery(id+"F0.imprint","IMPRINT",FACE,{"disambiguationData":[TD([[makeQuery(id+"F0.imprint","IMPRINT",EDGE,{"derivedFrom":subQ3}),1.0]])]});}
            var Q19;
            Q19=makeQuery(id+"F0.imprint","IMPRINT",FACE,{"disambiguationData":[TD([[makeQuery(id+"F0.imprint","IMPRINT",EDGE,{"derivedFrom":sQuery(id+"F0.wireOp",EDGE,"E0.bottom")}),1.0]])]});
            var Q20;
            Q20=makeQuery(id+"F0.imprint","IMPRINT",FACE,{"disambiguationData":[TD([[makeQuery(id+"F0.imprint","IMPRINT",EDGE,{"derivedFrom":sQuery(id+"F0.wireOp",EDGE,"E68.sketch_text.stroke-91")}),-1.0]])]});
            var Q21;
            Q21=makeQuery(id+"F0.imprint","IMPRINT",FACE,{"disambiguationData":[TD([[makeQuery(id+"F0.imprint","IMPRINT",EDGE,{"derivedFrom":sQuery(id+"F0.wireOp",EDGE,"E68.sketch_text.stroke-95")}),-1.0]])]});
            var Q22;
            Q22=makeQuery(id+"F0.imprint","IMPRINT",FACE,{"disambiguationData":[TD([[makeQuery(id+"F0.imprint","IMPRINT",EDGE,{"derivedFrom":sQuery(id+"F0.wireOp",EDGE,"E67.bottom")}),1.0]])]});
            var Q23;
            Q23=makeQuery(id+"F0.imprint","IMPRINT",FACE,{"disambiguationData":[TD([[makeQuery(id+"F0.imprint","IMPRINT",EDGE,{"derivedFrom":sQuery(id+"F0.wireOp",EDGE,"E68.sketch_text.stroke-0")}),-1.0]])]});
            var Q24;
            Q24=makeQuery(id+"F0.imprint","IMPRINT",FACE,{"disambiguationData":[TD([[makeQuery(id+"F0.imprint","IMPRINT",EDGE,{"derivedFrom":sQuery(id+"F0.wireOp",EDGE,"E68.sketch_text.stroke-11")}),-1.0]])]});
            var Q25;
            Q25=makeQuery(id+"F0.imprint","IMPRINT",FACE,{"disambiguationData":[TD([[makeQuery(id+"F0.imprint","IMPRINT",EDGE,{"derivedFrom":sQuery(id+"F0.wireOp",EDGE,"E68.sketch_text.stroke-25")}),-1.0]])]});
            var Q26;
            Q26=makeQuery(id+"F0.imprint","IMPRINT",FACE,{"disambiguationData":[TD([[makeQuery(id+"F0.imprint","IMPRINT",EDGE,{"derivedFrom":sQuery(id+"F0.wireOp",EDGE,"E68.sketch_text.stroke-37")}),-1.0]])]});
            var Q27;
            Q27=makeQuery(id+"F0.imprint","IMPRINT",FACE,{"disambiguationData":[TD([[makeQuery(id+"F0.imprint","IMPRINT",EDGE,{"derivedFrom":sQuery(id+"F0.wireOp",EDGE,"E68.sketch_text.stroke-50")}),-1.0]])]});
            var Q28;
            Q28=makeQuery(id+"F0.imprint","IMPRINT",FACE,{"disambiguationData":[TD([[makeQuery(id+"F0.imprint","IMPRINT",EDGE,{"derivedFrom":sQuery(id+"F0.wireOp",EDGE,"E68.sketch_text.stroke-57")}),-1.0]])]});
            var Q29;
            Q29=makeQuery(id+"F0.imprint","IMPRINT",FACE,{"disambiguationData":[TD([[makeQuery(id+"F0.imprint","IMPRINT",EDGE,{"derivedFrom":sQuery(id+"F0.wireOp",EDGE,"E68.sketch_text.stroke-61")}),-1.0]])]});
            var Q30;
            {var subQ3=sQuery(id+"F0.wireOp",EDGE,"E12.bottom");Q30=makeQuery(id+"F0.imprint","IMPRINT",FACE,{"disambiguationData":[TD([[makeQuery(id+"F0.imprint","IMPRINT",EDGE,{"derivedFrom":subQ3}),1.0]])]});}
            var Q31;
            {var subQ0=sQuery(id+"F0.wireOp",EDGE,"E29.bottom");Q31=makeQuery(id+"F0.imprint","IMPRINT",FACE,{"disambiguationData":[TD([[makeQuery(id+"F0.imprint","IMPRINT",EDGE,{"derivedFrom":subQ0}),-1.0]])]});}
            var Q32;
            {var subQ0=sQuery(id+"F0.wireOp",EDGE,"E21.bottom");Q32=makeQuery(id+"F0.imprint","IMPRINT",FACE,{"disambiguationData":[TD([[makeQuery(id+"F0.imprint","IMPRINT",EDGE,{"derivedFrom":subQ0}),-1.0]])]});}
            var Q33;
            {var subQ0=sQuery(id+"F0.wireOp",EDGE,"E39.bottom");Q33=makeQuery(id+"F0.imprint","IMPRINT",FACE,{"disambiguationData":[TD([[makeQuery(id+"F0.imprint","IMPRINT",EDGE,{"derivedFrom":subQ0}),-1.0]])]});}
            var Q34;
            {var subQ0=sQuery(id+"F0.wireOp",EDGE,"E59.bottom");Q34=makeQuery(id+"F0.imprint","IMPRINT",FACE,{"disambiguationData":[TD([[makeQuery(id+"F0.imprint","IMPRINT",EDGE,{"derivedFrom":subQ0}),-1.0]])]});}
            var Q35;
            {var subQ0=sQuery(id+"F0.wireOp",EDGE,"E1.bottom");Q35=makeQuery(id+"F0.imprint","IMPRINT",FACE,{"disambiguationData":[TD([[makeQuery(id+"F0.imprint","IMPRINT",EDGE,{"derivedFrom":subQ0}),-1.0]])]});}
            var Q36;
            {var subQ0=sQuery(id+"F0.wireOp",EDGE,"E43.bottom");Q36=makeQuery(id+"F0.imprint","IMPRINT",FACE,{"disambiguationData":[TD([[makeQuery(id+"F0.imprint","IMPRINT",EDGE,{"derivedFrom":subQ0}),-1.0]])]});}
            var Q37;
            {var subQ0=sQuery(id+"F0.wireOp",EDGE,"E5.bottom");Q37=makeQuery(id+"F0.imprint","IMPRINT",FACE,{"disambiguationData":[TD([[makeQuery(id+"F0.imprint","IMPRINT",EDGE,{"derivedFrom":subQ0}),-1.0]])]});}
            var Q38;
            {var subQ0=sQuery(id+"F0.wireOp",EDGE,"E47.bottom");Q38=makeQuery(id+"F0.imprint","IMPRINT",FACE,{"disambiguationData":[TD([[makeQuery(id+"F0.imprint","IMPRINT",EDGE,{"derivedFrom":subQ0}),-1.0]])]});}
            var Q39;
            {var subQ0=sQuery(id+"F0.wireOp",EDGE,"E9.bottom");Q39=makeQuery(id+"F0.imprint","IMPRINT",FACE,{"disambiguationData":[TD([[makeQuery(id+"F0.imprint","IMPRINT",EDGE,{"derivedFrom":subQ0}),-1.0]])]});}
            var Q40;
            {var subQ0=sQuery(id+"F0.wireOp",EDGE,"E17.bottom");Q40=makeQuery(id+"F0.imprint","IMPRINT",FACE,{"disambiguationData":[TD([[makeQuery(id+"F0.imprint","IMPRINT",EDGE,{"derivedFrom":subQ0}),-1.0]])]});}
            var Q41;
            {var subQ0=sQuery(id+"F0.wireOp",EDGE,"E35.bottom");Q41=makeQuery(id+"F0.imprint","IMPRINT",FACE,{"disambiguationData":[TD([[makeQuery(id+"F0.imprint","IMPRINT",EDGE,{"derivedFrom":subQ0}),-1.0]])]});}
            var Q42;
            {var subQ0=sQuery(id+"F0.wireOp",EDGE,"E13.bottom");Q42=makeQuery(id+"F0.imprint","IMPRINT",FACE,{"disambiguationData":[TD([[makeQuery(id+"F0.imprint","IMPRINT",EDGE,{"derivedFrom":subQ0}),-1.0]])]});}
            var Q43;
            {var subQ0=sQuery(id+"F0.wireOp",EDGE,"E25.bottom");Q43=makeQuery(id+"F0.imprint","IMPRINT",FACE,{"disambiguationData":[TD([[makeQuery(id+"F0.imprint","IMPRINT",EDGE,{"derivedFrom":subQ0}),-1.0]])]});}
            var Q44;
            {var subQ0=sQuery(id+"F0.wireOp",EDGE,"E13.top");Q44=makeQuery(id+"F0.imprint","IMPRINT",FACE,{"disambiguationData":[TD([[makeQuery(id+"F0.imprint","IMPRINT",EDGE,{"derivedFrom":subQ0}),1.0]])]});}
            var Q45;
            {var subQ0=sQuery(id+"F0.wireOp",EDGE,"E51.bottom");Q45=makeQuery(id+"F0.imprint","IMPRINT",FACE,{"disambiguationData":[TD([[makeQuery(id+"F0.imprint","IMPRINT",EDGE,{"derivedFrom":subQ0}),-1.0]])]});}
            var Q46;
            {var subQ0=sQuery(id+"F0.wireOp",EDGE,"E55.bottom");Q46=makeQuery(id+"F0.imprint","IMPRINT",FACE,{"disambiguationData":[TD([[makeQuery(id+"F0.imprint","IMPRINT",EDGE,{"derivedFrom":subQ0}),-1.0]])]});}
            extrude(context, id + "F2", {"entities" : qUnion([Q0, Q1, Q2, Q3, Q4, Q5, Q6, Q7, Q8, Q9, Q10, Q11, Q12, Q13, Q14, Q15, Q16, Q17, Q18, Q19, Q20, Q21, Q22, Q23, Q24, Q25, Q26, Q27, Q28, Q29, Q30, Q31, Q32, Q33, Q34, Q35, Q36, Q37, Q38, Q39, Q40, Q41, Q42, Q43, Q44, Q45, Q46]), "operationType" : NewBodyOperationType.REMOVE, "oppositeDirection" : true, "depth" : 3.8 * mm, "offsetDistance" : 25.4 * mm});
        }
        {
            var Q0;
            Q0=makeQuery(id+"F0.imprint","IMPRINT",FACE,{"disambiguationData":[TD([[makeQuery(id+"F0.imprint","IMPRINT",EDGE,{"derivedFrom":sQuery(id+"F0.wireOp",EDGE,"E68.sketch_text.stroke-11")}),-1.0]])]});
            var Q1;
            Q1=makeQuery(id+"F0.imprint","IMPRINT",FACE,{"disambiguationData":[TD([[makeQuery(id+"F0.imprint","IMPRINT",EDGE,{"derivedFrom":sQuery(id+"F0.wireOp",EDGE,"E68.sketch_text.stroke-25")}),-1.0]])]});
            var Q2;
            Q2=makeQuery(id+"F0.imprint","IMPRINT",FACE,{"disambiguationData":[TD([[makeQuery(id+"F0.imprint","IMPRINT",EDGE,{"derivedFrom":sQuery(id+"F0.wireOp",EDGE,"E68.sketch_text.stroke-37")}),-1.0]])]});
            var Q3;
            Q3=makeQuery(id+"F0.imprint","IMPRINT",FACE,{"disambiguationData":[TD([[makeQuery(id+"F0.imprint","IMPRINT",EDGE,{"derivedFrom":sQuery(id+"F0.wireOp",EDGE,"E68.sketch_text.stroke-0")}),-1.0]])]});
            var Q4;
            Q4=makeQuery(id+"F0.imprint","IMPRINT",FACE,{"disambiguationData":[TD([[makeQuery(id+"F0.imprint","IMPRINT",EDGE,{"derivedFrom":sQuery(id+"F0.wireOp",EDGE,"E68.sketch_text.stroke-57")}),-1.0]])]});
            var Q5;
            Q5=makeQuery(id+"F0.imprint","IMPRINT",FACE,{"disambiguationData":[TD([[makeQuery(id+"F0.imprint","IMPRINT",EDGE,{"derivedFrom":sQuery(id+"F0.wireOp",EDGE,"E68.sketch_text.stroke-50")}),-1.0]])]});
            var Q6;
            Q6=makeQuery(id+"F0.imprint","IMPRINT",FACE,{"disambiguationData":[TD([[makeQuery(id+"F0.imprint","IMPRINT",EDGE,{"derivedFrom":sQuery(id+"F0.wireOp",EDGE,"E68.sketch_text.stroke-61")}),-1.0]])]});
            var Q7;
            Q7=makeQuery(id+"F0.imprint","IMPRINT",FACE,{"disambiguationData":[TD([[makeQuery(id+"F0.imprint","IMPRINT",EDGE,{"derivedFrom":sQuery(id+"F0.wireOp",EDGE,"E68.sketch_text.stroke-68")}),-1.0]])]});
            var Q8;
            Q8=makeQuery(id+"F0.imprint","IMPRINT",FACE,{"disambiguationData":[TD([[makeQuery(id+"F0.imprint","IMPRINT",EDGE,{"derivedFrom":sQuery(id+"F0.wireOp",EDGE,"E68.sketch_text.stroke-72")}),-1.0]])]});
            var Q9;
            Q9=makeQuery(id+"F0.imprint","IMPRINT",FACE,{"disambiguationData":[TD([[makeQuery(id+"F0.imprint","IMPRINT",EDGE,{"derivedFrom":sQuery(id+"F0.wireOp",EDGE,"E68.sketch_text.stroke-76")}),-1.0]])]});
            var Q10;
            Q10=makeQuery(id+"F0.imprint","IMPRINT",FACE,{"disambiguationData":[TD([[makeQuery(id+"F0.imprint","IMPRINT",EDGE,{"derivedFrom":sQuery(id+"F0.wireOp",EDGE,"E68.sketch_text.stroke-83")}),-1.0]])]});
            var Q11;
            Q11=makeQuery(id+"F0.imprint","IMPRINT",FACE,{"disambiguationData":[TD([[makeQuery(id+"F0.imprint","IMPRINT",EDGE,{"derivedFrom":sQuery(id+"F0.wireOp",EDGE,"E68.sketch_text.stroke-87")}),-1.0]])]});
            var Q12;
            Q12=makeQuery(id+"F0.imprint","IMPRINT",FACE,{"disambiguationData":[TD([[makeQuery(id+"F0.imprint","IMPRINT",EDGE,{"derivedFrom":sQuery(id+"F0.wireOp",EDGE,"E68.sketch_text.stroke-91")}),-1.0]])]});
            var Q13;
            Q13=makeQuery(id+"F0.imprint","IMPRINT",FACE,{"disambiguationData":[TD([[makeQuery(id+"F0.imprint","IMPRINT",EDGE,{"derivedFrom":sQuery(id+"F0.wireOp",EDGE,"E68.sketch_text.stroke-95")}),-1.0]])]});
            extrude(context, id + "F3", {"entities" : qUnion([Q0, Q1, Q2, Q3, Q4, Q5, Q6, Q7, Q8, Q9, Q10, Q11, Q12, Q13]), "operationType" : NewBodyOperationType.ADD, "oppositeDirection" : true, "depth" : 5.08 * mm, "offsetDistance" : 25.4 * mm});
        }
        {
            var Q0;
            Q0=makeQuery(id+"F0.imprint","IMPRINT",FACE,{"disambiguationData":[TD([[makeQuery(id+"F0.imprint","IMPRINT",EDGE,{"derivedFrom":sQuery(id+"F0.wireOp",EDGE,"E68.sketch_text.stroke-11")}),-1.0]])]});
            var Q1;
            Q1=makeQuery(id+"F0.imprint","IMPRINT",FACE,{"disambiguationData":[TD([[makeQuery(id+"F0.imprint","IMPRINT",EDGE,{"derivedFrom":sQuery(id+"F0.wireOp",EDGE,"E68.sketch_text.stroke-0")}),-1.0]])]});
            var Q2;
            Q2=makeQuery(id+"F0.imprint","IMPRINT",FACE,{"disambiguationData":[TD([[makeQuery(id+"F0.imprint","IMPRINT",EDGE,{"derivedFrom":sQuery(id+"F0.wireOp",EDGE,"E68.sketch_text.stroke-37")}),-1.0]])]});
            var Q3;
            Q3=makeQuery(id+"F0.imprint","IMPRINT",FACE,{"disambiguationData":[TD([[makeQuery(id+"F0.imprint","IMPRINT",EDGE,{"derivedFrom":sQuery(id+"F0.wireOp",EDGE,"E68.sketch_text.stroke-25")}),-1.0]])]});
            var Q4;
            Q4=makeQuery(id+"F0.imprint","IMPRINT",FACE,{"disambiguationData":[TD([[makeQuery(id+"F0.imprint","IMPRINT",EDGE,{"derivedFrom":sQuery(id+"F0.wireOp",EDGE,"E68.sketch_text.stroke-57")}),-1.0]])]});
            var Q5;
            Q5=makeQuery(id+"F0.imprint","IMPRINT",FACE,{"disambiguationData":[TD([[makeQuery(id+"F0.imprint","IMPRINT",EDGE,{"derivedFrom":sQuery(id+"F0.wireOp",EDGE,"E68.sketch_text.stroke-50")}),-1.0]])]});
            var Q6;
            Q6=makeQuery(id+"F0.imprint","IMPRINT",FACE,{"disambiguationData":[TD([[makeQuery(id+"F0.imprint","IMPRINT",EDGE,{"derivedFrom":sQuery(id+"F0.wireOp",EDGE,"E68.sketch_text.stroke-61")}),-1.0]])]});
            var Q7;
            Q7=makeQuery(id+"F0.imprint","IMPRINT",FACE,{"disambiguationData":[TD([[makeQuery(id+"F0.imprint","IMPRINT",EDGE,{"derivedFrom":sQuery(id+"F0.wireOp",EDGE,"E68.sketch_text.stroke-68")}),-1.0]])]});
            var Q8;
            Q8=makeQuery(id+"F0.imprint","IMPRINT",FACE,{"disambiguationData":[TD([[makeQuery(id+"F0.imprint","IMPRINT",EDGE,{"derivedFrom":sQuery(id+"F0.wireOp",EDGE,"E68.sketch_text.stroke-72")}),-1.0]])]});
            var Q9;
            Q9=makeQuery(id+"F0.imprint","IMPRINT",FACE,{"disambiguationData":[TD([[makeQuery(id+"F0.imprint","IMPRINT",EDGE,{"derivedFrom":sQuery(id+"F0.wireOp",EDGE,"E68.sketch_text.stroke-76")}),-1.0]])]});
            var Q10;
            Q10=makeQuery(id+"F0.imprint","IMPRINT",FACE,{"disambiguationData":[TD([[makeQuery(id+"F0.imprint","IMPRINT",EDGE,{"derivedFrom":sQuery(id+"F0.wireOp",EDGE,"E68.sketch_text.stroke-83")}),-1.0]])]});
            var Q11;
            Q11=makeQuery(id+"F0.imprint","IMPRINT",FACE,{"disambiguationData":[TD([[makeQuery(id+"F0.imprint","IMPRINT",EDGE,{"derivedFrom":sQuery(id+"F0.wireOp",EDGE,"E68.sketch_text.stroke-95")}),-1.0]])]});
            var Q12;
            Q12=makeQuery(id+"F0.imprint","IMPRINT",FACE,{"disambiguationData":[TD([[makeQuery(id+"F0.imprint","IMPRINT",EDGE,{"derivedFrom":sQuery(id+"F0.wireOp",EDGE,"E68.sketch_text.stroke-87")}),-1.0]])]});
            var Q13;
            Q13=makeQuery(id+"F0.imprint","IMPRINT",FACE,{"disambiguationData":[TD([[makeQuery(id+"F0.imprint","IMPRINT",EDGE,{"derivedFrom":sQuery(id+"F0.wireOp",EDGE,"E68.sketch_text.stroke-91")}),-1.0]])]});
            extrude(context, id + "F4", {"entities" : qUnion([Q0, Q1, Q2, Q3, Q4, Q5, Q6, Q7, Q8, Q9, Q10, Q11, Q12, Q13]), "operationType" : NewBodyOperationType.ADD, "depth" : 3.8 * mm, "offsetDistance" : 25.4 * mm});
        }
        {
            var Q0;
            Q0=makeQuery(id+"F1.opExtrude","SWEPT_BODY",BODY,{"disambiguationData":[OSD([sQuery(id+"F0.wireOp",EDGE,"E66.bottom"),sQuery(id+"F0.wireOp",EDGE,"E66.top"),sQuery(id+"F0.wireOp",EDGE,"E66.left"),sQuery(id+"F0.wireOp",EDGE,"E66.right")])]});
            var Q1;
            Q1=makeQuery(id+"F1.opExtrude","CAP_VERTEX",VERTEX,{"disambiguationData":[OSD([sQuery(id+"F0.wireOp",EDGE,"E66.bottom"),sQuery(id+"F0.wireOp",EDGE,"E66.right")])],"isStart":false});
            transform(context, id + "F5", {"entities" : qUnion([Q0]), "transformType" : TransformType.SCALE_UNIFORMLY, "scale" : .5, "scalePoint" : qUnion([Q1]), "makeCopy" : false});
        }
    });
